# Revit family: Edge_TB42_G_Top_Hung_Standard
name_source: partatom
category: Windows
revit_build: Autodesk Revit 2014 (Build: 20130308_1515(x64)
units: mm (PartAtom-declared; Revit-internal decimal feet)

## types (12) — shared parameters
Aluminium Thickness = 1 mm  [stored 0.00328084 ft]
Bead SG Gap = 13 mm
Bottom Hung = No
Casement Dimension = 42 mm  [stored 0.137795 ft]
Custom Sash Height Bottom = 569 mm  [stored 1.8668 ft]
Custom Sash Height Top = 569 mm  [stored 1.8668 ft]
Custom Window Height = 1190 mm  [stored 3.9042 ft]
DG Extrusion Start = 11 mm  [stored 0.0360892 ft]
DG Gasket Finish = Double Glazing Gasket Material
DG Thickness Calc = 4 mm  [stored 0.0131234 ft]
Default Sill Height = 800 mm  [stored 2.62467 ft]
Depth Bead = 28 mm  [stored 0.0918635 ft]
Description = Thermal break casement windows (42mm), Type G top hung
Frame Center Offset = 21 mm  [stored 0.0688976 ft]
Height = 1200 mm  [stored 3.93701 ft]
Height Panel 1 = 555 mm  [stored 1.82087 ft]
Height Panel 2 = 555 mm  [stored 1.82087 ft]
Height Panel 4 = 1140 mm  [stored 3.74016 ft]
Height Sash 1 = 539 mm
Height Sash 2 = 539 mm
Height Sash Bottom Opening = 569 mm  [stored 1.8668 ft]
Height Sash Top Opening = 569 mm  [stored 1.8668 ft]
Length Mullion = 1200 mm  [stored 3.93701 ft]
Limit Fixed Pane Height Max = 1800 mm
Limit Fixed Pane Height Min = 200 mm  [stored 0.656168 ft]
Limit Fixed Pane Width Max = 1500 mm
Limit Fixed Pane Width Min = 200 mm  [stored 0.656168 ft]
Limit Sash Bottom Height Max Based On Top Sash = 1229 mm
Limit Sash Height Bottom Max = 1200 mm  [stored 3.93701 ft]
Limit Sash Height Bottom Min = 300 mm  [stored 0.984252 ft]
Limit Sash Height Top Max = 1200 mm  [stored 3.93701 ft]
Limit Sash Height Top Min = 300 mm  [stored 0.984252 ft]
Limit Sash Width Max = 1500 mm
Limit Sash Width Min = 300 mm  [stored 0.984252 ft]
Limit Window Height Max = 1860 mm
Manufacturer = Crealco
Max System DG One Piece Thickness = 6 mm  [stored 0.019685 ft]
Max System DG Unit Thickness = 25 mm  [stored 0.082021 ft]
Model = Edge
Offset Bead SG Center Reversed = 21 mm  [stored 0.0688976 ft]
Offset Sash 1 Top = 23 mm  [stored 0.0754593 ft]
Offset Sash 2 Top = 608 mm  [stored 1.99475 ft]
Offset Sash Left = 23 mm  [stored 0.0754593 ft]
Offset Transom 1 Top = 585 mm  [stored 1.91929 ft]
Offset Window Exterior = 21 mm  [stored 0.0688976 ft]
Rough Width = 16 mm  [stored 0.0524934 ft]
SG Gasket Thickness = 6 mm  [stored 0.019685 ft]
Sash Center Offset = 18 mm
Sash Overlap = 7 mm  [stored 0.0229659 ft]
Sash Spacing Inner = 8 mm  [stored 0.0262467 ft]
Top Hung = Yes
URL = http://www.crealco.co.za
Wall Closure = By host
Width Bead = 15 mm  [stored 0.0492126 ft]
Width Profile = 30 mm  [stored 0.0984252 ft]
zero-valued in all types: Window Exterior Offset

## per-type parameters (varying)
- EDGE-1212DT-1000Pa: Area Pane Left Bottom=0.25 m²; Area Pane Left Top=0.25 m²; Area Pane Right=0.6 m²; Clearvue Insulated LowE SHGC Value=0.616; Clearvue Insulated LowE U Value=3.5; Clearvue Insulated SHGC Value=0.677; Clearvue Insulated U Value=4.16; Clearvue SHGC Value=0.749; Clearvue U Value=7.15; Custom Sash Width=569 mm  [stored 1.8668 ft]; Custom Windload=1000 mm  [stored 3.28084 ft]; Custom Window Width=1190 mm  [stored 3.9042 ft]; Depth Mullion=0 mm  [stored 0 ft]; Energy Advantage SHGC Value=0.671; Energy Advantage U Value=5.33; Has Stiffener Cap=No; Intruderprufe Insulated LowE SHGC Value=0.561; Intruderprufe Insulated LowE U Value=3.45; Intruderprufe Insulated SHGC Value=0.621; Intruderprufe Insulated U Value=4.1; Intruderprufe LowE SHGC Value=0.627; Intruderprufe LowE U Value=5.33; Intruderprufe SHGC Value=0.699; Intruderprufe U Value=7.03; Length Transom=555 mm  [stored 1.82087 ft]; Limit Window Width Max=2145 mm; Limit Window Width Min=845 mm  [stored 2.77231 ft]; Max Pane Area=0.6 m²; Mullion Depth Windload Based=0 mm  [stored 0 ft]; Offset Mullion Left=585 mm  [stored 1.91929 ft]; Offset Panel 4 Left=615 mm  [stored 2.01772 ft]; Width=1190 mm  [stored 3.9042 ft]; Width Panel 1=555 mm  [stored 1.82087 ft]; Width Panel 2=555 mm  [stored 1.82087 ft]; Width Panel 4=545 mm; Width Sash 1=539 mm; Width Sash 2=539 mm; Width Sash Opening=569 mm  [stored 1.8668 ft]; Windload Design=1000 mm  [stored 3.28084 ft]
- EDGE-1512DT-1000Pa: Area Pane Left Bottom=0.25 m²; Area Pane Left Top=0.25 m²; Area Pane Right=0.94 m²; Clearvue Insulated LowE SHGC Value=0.71; Clearvue Insulated LowE U Value=3.61; Clearvue Insulated SHGC Value=0.781; Clearvue Insulated U Value=4.38; Clearvue SHGC Value=0.868; Clearvue U Value=7.8; Custom Sash Width=569 mm  [stored 1.8668 ft]; Custom Windload=1000 mm  [stored 3.28084 ft]; Custom Window Width=1490 mm; Depth Mullion=0 mm  [stored 0 ft]; Energy Advantage SHGC Value=0.776; Energy Advantage U Value=5.67; Has Stiffener Cap=No; Intruderprufe Insulated LowE SHGC Value=0.648; Intruderprufe Insulated LowE U Value=3.55; Intruderprufe Insulated SHGC Value=0.717; Intruderprufe Insulated U Value=4.32; Intruderprufe LowE SHGC Value=0.724; Intruderprufe LowE U Value=5.64; Intruderprufe SHGC Value=0.81; Intruderprufe U Value=7.66; Length Transom=555 mm  [stored 1.82087 ft]; Limit Window Width Max=2145 mm; Limit Window Width Min=845 mm  [stored 2.77231 ft]; Max Pane Area=0.94 m²; Mullion Depth Windload Based=0 mm  [stored 0 ft]; Offset Mullion Left=585 mm  [stored 1.91929 ft]; Offset Panel 4 Left=615 mm  [stored 2.01772 ft]; Width=1490 mm; Width Panel 1=555 mm  [stored 1.82087 ft]; Width Panel 2=555 mm  [stored 1.82087 ft]; Width Panel 4=845 mm  [stored 2.77231 ft]; Width Sash 1=539 mm; Width Sash 2=539 mm; Width Sash Opening=569 mm  [stored 1.8668 ft]; Windload Design=1000 mm  [stored 3.28084 ft]
- EDGE-1812DT-1000Pa: Area Pane Left Bottom=0.39 m²; Area Pane Left Top=0.39 m²; Area Pane Right=0.96 m²; Clearvue Insulated LowE SHGC Value=0.665; Clearvue Insulated LowE U Value=3.35; Clearvue Insulated SHGC Value=0.731; Clearvue Insulated U Value=4.08; Clearvue SHGC Value=0.813; Clearvue U Value=7.26; Custom Sash Width=854 mm  [stored 2.80184 ft]; Custom Windload=1000 mm  [stored 3.28084 ft]; Custom Window Width=1790 mm; Depth Mullion=0 mm  [stored 0 ft]; Energy Advantage SHGC Value=0.728; Energy Advantage U Value=5.26; Has Stiffener Cap=No; Intruderprufe Insulated LowE SHGC Value=0.606; Intruderprufe Insulated LowE U Value=3.3; Intruderprufe Insulated SHGC Value=0.679; Intruderprufe Insulated U Value=4.02; Intruderprufe LowE SHGC Value=0.679; Intruderprufe LowE U Value=5.24; Intruderprufe SHGC Value=0.76; Intruderprufe U Value=7.13; Length Transom=840 mm  [stored 2.75591 ft]; Limit Window Width Max=2430 mm; Limit Window Width Min=1130 mm  [stored 3.70735 ft]; Max Pane Area=0.96 m²; Mullion Depth Windload Based=0 mm  [stored 0 ft]; Offset Mullion Left=870 mm  [stored 2.85433 ft]; Offset Panel 4 Left=900 mm  [stored 2.95276 ft]; Width=1790 mm; Width Panel 1=840 mm  [stored 2.75591 ft]; Width Panel 2=840 mm  [stored 2.75591 ft]; Width Panel 4=860 mm; Width Sash 1=824 mm; Width Sash 2=824 mm; Width Sash Opening=854 mm  [stored 2.80184 ft]; Windload Design=1000 mm  [stored 3.28084 ft]
- EDGE-2412DT-1000Pa: Area Pane Left Bottom=0.39 m²; Area Pane Left Top=0.39 m²; Area Pane Right=1.64 m²; Clearvue Insulated LowE SHGC Value=0.533; Clearvue Insulated LowE U Value=2.39; Clearvue Insulated SHGC Value=0.586; Clearvue Insulated U Value=2.98; Clearvue SHGC Value=0; Clearvue U Value=7.9; Custom Sash Width=854 mm  [stored 2.80184 ft]; Custom Windload=1000 mm  [stored 3.28084 ft]; Custom Window Width=2390 mm; Depth Mullion=0 mm  [stored 0 ft]; Energy Advantage SHGC Value=0; Energy Advantage U Value=7.9; Has Stiffener Cap=No; Intruderprufe Insulated LowE SHGC Value=0.486; Intruderprufe Insulated LowE U Value=2.35; Intruderprufe Insulated SHGC Value=0.539; Intruderprufe Insulated U Value=2.93; Intruderprufe LowE SHGC Value=0.546; Intruderprufe LowE U Value=3.87; Intruderprufe SHGC Value=0.613; Intruderprufe U Value=5.42; Length Transom=840 mm  [stored 2.75591 ft]; Limit Window Width Max=2430 mm; Limit Window Width Min=1130 mm  [stored 3.70735 ft]; Max Pane Area=1.64 m²; Mullion Depth Windload Based=0 mm  [stored 0 ft]; Offset Mullion Left=870 mm  [stored 2.85433 ft]; Offset Panel 4 Left=900 mm  [stored 2.95276 ft]; Width=2390 mm; Width Panel 1=840 mm  [stored 2.75591 ft]; Width Panel 2=840 mm  [stored 2.75591 ft]; Width Panel 4=1460 mm; Width Sash 1=824 mm; Width Sash 2=824 mm; Width Sash Opening=854 mm  [stored 2.80184 ft]; Windload Design=1000 mm  [stored 3.28084 ft]
- EDGE-1212DT-1500Pa: Area Pane Left Bottom=0.25 m²; Area Pane Left Top=0.25 m²; Area Pane Right=0.6 m²; Clearvue Insulated LowE SHGC Value=0.616; Clearvue Insulated LowE U Value=3.5; Clearvue Insulated SHGC Value=0.677; Clearvue Insulated U Value=4.16; Clearvue SHGC Value=0.749; Clearvue U Value=7.15; Custom Sash Width=569 mm  [stored 1.8668 ft]; Custom Windload=1500 mm; Custom Window Width=1190 mm  [stored 3.9042 ft]; Depth Mullion=0 mm  [stored 0 ft]; Energy Advantage SHGC Value=0.671; Energy Advantage U Value=5.33; Has Stiffener Cap=No; Intruderprufe Insulated LowE SHGC Value=0.561; Intruderprufe Insulated LowE U Value=3.45; Intruderprufe Insulated SHGC Value=0.621; Intruderprufe Insulated U Value=4.1; Intruderprufe LowE SHGC Value=0.627; Intruderprufe LowE U Value=5.33; Intruderprufe SHGC Value=0.699; Intruderprufe U Value=7.03; Length Transom=555 mm  [stored 1.82087 ft]; Limit Window Width Max=2145 mm; Limit Window Width Min=845 mm  [stored 2.77231 ft]; Max Pane Area=0.6 m²; Mullion Depth Windload Based=0 mm  [stored 0 ft]; Offset Mullion Left=585 mm  [stored 1.91929 ft]; Offset Panel 4 Left=615 mm  [stored 2.01772 ft]; Width=1190 mm  [stored 3.9042 ft]; Width Panel 1=555 mm  [stored 1.82087 ft]; Width Panel 2=555 mm  [stored 1.82087 ft]; Width Panel 4=545 mm; Width Sash 1=539 mm; Width Sash 2=539 mm; Width Sash Opening=569 mm  [stored 1.8668 ft]; Windload Design=1500 mm
- EDGE-1212DT-2000Pa: Area Pane Left Bottom=0.25 m²; Area Pane Left Top=0.25 m²; Area Pane Right=0.6 m²; Clearvue Insulated LowE SHGC Value=0.667; Clearvue Insulated LowE U Value=3.16; Clearvue Insulated SHGC Value=0.733; Clearvue Insulated U Value=3.83; Clearvue SHGC Value=0.812; Clearvue U Value=6.73; Custom Sash Width=569 mm  [stored 1.8668 ft]; Custom Windload=2000 mm; Custom Window Width=1190 mm  [stored 3.9042 ft]; Depth Mullion=1 mm  [stored 0.00328084 ft]; Energy Advantage SHGC Value=0.726; Energy Advantage U Value=4.9; Has Stiffener Cap=Yes; Intruderprufe Insulated LowE SHGC Value=0.608; Intruderprufe Insulated LowE U Value=3.11; Intruderprufe Insulated SHGC Value=0.673; Intruderprufe Insulated U Value=3.77; Intruderprufe LowE SHGC Value=0.678; Intruderprufe LowE U Value=4.88; Intruderprufe SHGC Value=0.759; Intruderprufe U Value=6.61; Length Transom=555 mm  [stored 1.82087 ft]; Limit Window Width Max=2145 mm; Limit Window Width Min=845 mm  [stored 2.77231 ft]; Max Pane Area=0.6 m²; Mullion Depth Windload Based=1 mm  [stored 0.00328084 ft]; Offset Mullion Left=585 mm  [stored 1.91929 ft]; Offset Panel 4 Left=615 mm  [stored 2.01772 ft]; Width=1190 mm  [stored 3.9042 ft]; Width Panel 1=555 mm  [stored 1.82087 ft]; Width Panel 2=555 mm  [stored 1.82087 ft]; Width Panel 4=545 mm; Width Sash 1=539 mm; Width Sash 2=539 mm; Width Sash Opening=569 mm  [stored 1.8668 ft]; Windload Design=2000 mm
- EDGE-1512DT-2000Pa: Area Pane Left Bottom=0.25 m²; Area Pane Left Top=0.25 m²; Area Pane Right=0.94 m²; Clearvue Insulated LowE SHGC Value=0.753; Clearvue Insulated LowE U Value=3.31; Clearvue Insulated SHGC Value=0.829; Clearvue Insulated U Value=4.1; Clearvue SHGC Value=0.922; Clearvue U Value=7.43; Custom Sash Width=569 mm  [stored 1.8668 ft]; Custom Windload=2000 mm; Custom Window Width=1490 mm; Depth Mullion=1 mm  [stored 0.00328084 ft]; Energy Advantage SHGC Value=0.824; Energy Advantage U Value=5.3; Has Stiffener Cap=Yes; Intruderprufe Insulated LowE SHGC Value=0.688; Intruderprufe Insulated LowE U Value=3.26; Intruderprufe Insulated SHGC Value=0.762; Intruderprufe Insulated U Value=4.03; Intruderprufe LowE SHGC Value=0.768; Intruderprufe LowE U Value=5.26; Intruderprufe SHGC Value=0.862; Intruderprufe U Value=7.3; Length Transom=555 mm  [stored 1.82087 ft]; Limit Window Width Max=2145 mm; Limit Window Width Min=845 mm  [stored 2.77231 ft]; Max Pane Area=0.94 m²; Mullion Depth Windload Based=1 mm  [stored 0.00328084 ft]; Offset Mullion Left=585 mm  [stored 1.91929 ft]; Offset Panel 4 Left=615 mm  [stored 2.01772 ft]; Width=1490 mm; Width Panel 1=555 mm  [stored 1.82087 ft]; Width Panel 2=555 mm  [stored 1.82087 ft]; Width Panel 4=845 mm  [stored 2.77231 ft]; Width Sash 1=539 mm; Width Sash 2=539 mm; Width Sash Opening=569 mm  [stored 1.8668 ft]; Windload Design=2000 mm
- EDGE-1812DT-1500Pa: Area Pane Left Bottom=0.39 m²; Area Pane Left Top=0.39 m²; Area Pane Right=0.96 m²; Clearvue Insulated LowE SHGC Value=0.699; Clearvue Insulated LowE U Value=3.12; Clearvue Insulated SHGC Value=0.769; Clearvue Insulated U Value=3.86; Clearvue SHGC Value=0.855; Clearvue U Value=6.98; Custom Sash Width=854 mm  [stored 2.80184 ft]; Custom Windload=1500 mm; Custom Window Width=1790 mm; Depth Mullion=1 mm  [stored 0.00328084 ft]; Energy Advantage SHGC Value=0.765; Energy Advantage U Value=4.98; Has Stiffener Cap=Yes; Intruderprufe Insulated LowE SHGC Value=0.637; Intruderprufe Insulated LowE U Value=3.08; Intruderprufe Insulated SHGC Value=0.706; Intruderprufe Insulated U Value=3.8; Intruderprufe LowE SHGC Value=0.713; Intruderprufe LowE U Value=4.94; Intruderprufe SHGC Value=0.8; Intruderprufe U Value=6.85; Length Transom=840 mm  [stored 2.75591 ft]; Limit Window Width Max=2430 mm; Limit Window Width Min=1130 mm  [stored 3.70735 ft]; Max Pane Area=0.96 m²; Mullion Depth Windload Based=1 mm  [stored 0.00328084 ft]; Offset Mullion Left=870 mm  [stored 2.85433 ft]; Offset Panel 4 Left=900 mm  [stored 2.95276 ft]; Width=1790 mm; Width Panel 1=840 mm  [stored 2.75591 ft]; Width Panel 2=840 mm  [stored 2.75591 ft]; Width Panel 4=860 mm; Width Sash 1=824 mm; Width Sash 2=824 mm; Width Sash Opening=854 mm  [stored 2.80184 ft]; Windload Design=1500 mm
- EDGE-1812DT-2000Pa: Area Pane Left Bottom=0.39 m²; Area Pane Left Top=0.39 m²; Area Pane Right=0.96 m²; Clearvue Insulated LowE SHGC Value=0.699; Clearvue Insulated LowE U Value=3.12; Clearvue Insulated SHGC Value=0.769; Clearvue Insulated U Value=3.86; Clearvue SHGC Value=0.855; Clearvue U Value=6.98; Custom Sash Width=854 mm  [stored 2.80184 ft]; Custom Windload=2000 mm; Custom Window Width=1790 mm; Depth Mullion=1 mm  [stored 0.00328084 ft]; Energy Advantage SHGC Value=0.765; Energy Advantage U Value=4.98; Has Stiffener Cap=Yes; Intruderprufe Insulated LowE SHGC Value=0.637; Intruderprufe Insulated LowE U Value=3.08; Intruderprufe Insulated SHGC Value=0.706; Intruderprufe Insulated U Value=3.8; Intruderprufe LowE SHGC Value=0.713; Intruderprufe LowE U Value=4.94; Intruderprufe SHGC Value=0.8; Intruderprufe U Value=6.85; Length Transom=840 mm  [stored 2.75591 ft]; Limit Window Width Max=2430 mm; Limit Window Width Min=1130 mm  [stored 3.70735 ft]; Max Pane Area=0.96 m²; Mullion Depth Windload Based=1 mm  [stored 0.00328084 ft]; Offset Mullion Left=870 mm  [stored 2.85433 ft]; Offset Panel 4 Left=900 mm  [stored 2.95276 ft]; Width=1790 mm; Width Panel 1=840 mm  [stored 2.75591 ft]; Width Panel 2=840 mm  [stored 2.75591 ft]; Width Panel 4=860 mm; Width Sash 1=824 mm; Width Sash 2=824 mm; Width Sash Opening=854 mm  [stored 2.80184 ft]; Windload Design=2000 mm
- EDGE-2412DT-1500Pa: Area Pane Left Bottom=0.39 m²; Area Pane Left Top=0.39 m²; Area Pane Right=1.64 m²; Clearvue Insulated LowE SHGC Value=0.557; Clearvue Insulated LowE U Value=2.22; Clearvue Insulated SHGC Value=0.613; Clearvue Insulated U Value=2.82; Clearvue SHGC Value=0; Clearvue U Value=7.9; Custom Sash Width=854 mm  [stored 2.80184 ft]; Custom Windload=1500 mm; Custom Window Width=2390 mm; Depth Mullion=1 mm  [stored 0.00328084 ft]; Energy Advantage SHGC Value=0; Energy Advantage U Value=7.9; Has Stiffener Cap=Yes; Intruderprufe Insulated LowE SHGC Value=0.509; Intruderprufe Insulated LowE U Value=2.19; Intruderprufe Insulated SHGC Value=0.564; Intruderprufe Insulated U Value=2.77; Intruderprufe LowE SHGC Value=0.57; Intruderprufe LowE U Value=3.65; Intruderprufe SHGC Value=0.641; Intruderprufe U Value=5.21; Length Transom=840 mm  [stored 2.75591 ft]; Limit Window Width Max=2430 mm; Limit Window Width Min=1130 mm  [stored 3.70735 ft]; Max Pane Area=1.64 m²; Mullion Depth Windload Based=1 mm  [stored 0.00328084 ft]; Offset Mullion Left=870 mm  [stored 2.85433 ft]; Offset Panel 4 Left=900 mm  [stored 2.95276 ft]; Width=2390 mm; Width Panel 1=840 mm  [stored 2.75591 ft]; Width Panel 2=840 mm  [stored 2.75591 ft]; Width Panel 4=1460 mm; Width Sash 1=824 mm; Width Sash 2=824 mm; Width Sash Opening=854 mm  [stored 2.80184 ft]; Windload Design=1500 mm
- EDGE-2412DT-2000Pa: Area Pane Left Bottom=0.39 m²; Area Pane Left Top=0.39 m²; Area Pane Right=1.64 m²; Clearvue Insulated LowE SHGC Value=0.557; Clearvue Insulated LowE U Value=2.22; Clearvue Insulated SHGC Value=0.613; Clearvue Insulated U Value=2.82; Clearvue SHGC Value=0; Clearvue U Value=7.9; Custom Sash Width=854 mm  [stored 2.80184 ft]; Custom Windload=2000 mm; Custom Window Width=2390 mm; Depth Mullion=1 mm  [stored 0.00328084 ft]; Energy Advantage SHGC Value=0; Energy Advantage U Value=7.9; Has Stiffener Cap=Yes; Intruderprufe Insulated LowE SHGC Value=0.509; Intruderprufe Insulated LowE U Value=2.19; Intruderprufe Insulated SHGC Value=0.564; Intruderprufe Insulated U Value=2.77; Intruderprufe LowE SHGC Value=0.57; Intruderprufe LowE U Value=3.65; Intruderprufe SHGC Value=0.641; Intruderprufe U Value=5.21; Length Transom=840 mm  [stored 2.75591 ft]; Limit Window Width Max=2430 mm; Limit Window Width Min=1130 mm  [stored 3.70735 ft]; Max Pane Area=1.64 m²; Mullion Depth Windload Based=1 mm  [stored 0.00328084 ft]; Offset Mullion Left=870 mm  [stored 2.85433 ft]; Offset Panel 4 Left=900 mm  [stored 2.95276 ft]; Width=2390 mm; Width Panel 1=840 mm  [stored 2.75591 ft]; Width Panel 2=840 mm  [stored 2.75591 ft]; Width Panel 4=1460 mm; Width Sash 1=824 mm; Width Sash 2=824 mm; Width Sash Opening=854 mm  [stored 2.80184 ft]; Windload Design=2000 mm
- EDGE-1512DT-1500Pa: Area Pane Left Bottom=0.25 m²; Area Pane Left Top=0.25 m²; Area Pane Right=0.94 m²; Clearvue Insulated LowE SHGC Value=0.71; Clearvue Insulated LowE U Value=3.61; Clearvue Insulated SHGC Value=0.781; Clearvue Insulated U Value=4.38; Clearvue SHGC Value=0.868; Clearvue U Value=7.8; Custom Sash Width=569 mm  [stored 1.8668 ft]; Custom Windload=1500 mm; Custom Window Width=1490 mm; Depth Mullion=0 mm  [stored 0 ft]; Energy Advantage SHGC Value=0.776; Energy Advantage U Value=5.67; Has Stiffener Cap=No; Intruderprufe Insulated LowE SHGC Value=0.648; Intruderprufe Insulated LowE U Value=3.55; Intruderprufe Insulated SHGC Value=0.717; Intruderprufe Insulated U Value=4.32; Intruderprufe LowE SHGC Value=0.724; Intruderprufe LowE U Value=5.64; Intruderprufe SHGC Value=0.81; Intruderprufe U Value=7.66; Length Transom=555 mm  [stored 1.82087 ft]; Limit Window Width Max=2145 mm; Limit Window Width Min=845 mm  [stored 2.77231 ft]; Max Pane Area=0.94 m²; Mullion Depth Windload Based=0 mm  [stored 0 ft]; Offset Mullion Left=585 mm  [stored 1.91929 ft]; Offset Panel 4 Left=615 mm  [stored 2.01772 ft]; Width=1490 mm; Width Panel 1=555 mm  [stored 1.82087 ft]; Width Panel 2=555 mm  [stored 1.82087 ft]; Width Panel 4=845 mm  [stored 2.77231 ft]; Width Sash 1=539 mm; Width Sash 2=539 mm; Width Sash Opening=569 mm  [stored 1.8668 ft]; Windload Design=1500 mm

note: [stored X ft] marks values corroborated as IEEE doubles in the binary element streams (Revit-internal decimal feet)

## geometry (parser evidence)
native form markers: Blend x4, Extrusion x1, Sweep x25
no freeform markers — native parametric forms only
